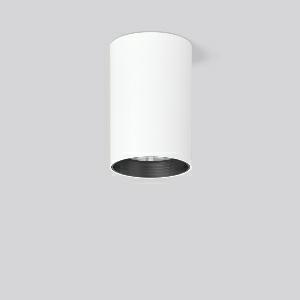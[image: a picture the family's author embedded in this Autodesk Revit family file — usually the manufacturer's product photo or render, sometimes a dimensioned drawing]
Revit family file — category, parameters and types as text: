
# Revit family: heledon_maxi_a_931221_002_3_a406
name_source: partatom
category: Lighting Fixtures
units: mm (PartAtom-declared; Revit-internal decimal feet)

## family parameters
Cut with Voids When Loaded = No
Host = Face
Light Source = No
Part Type = Normal
Room Calculation Point = No
Round Connector Dimension = Use Diameter
Shared = No

## types (1)
- HELEDON maxi A (1 x LED Modul 935, 2800 lm, 3500)
    Apparent Load = 25 VA
    Approval mark = CE
    CIE Flux Codes = 96 100 100 100 100
    Color Rendering = 92
    Color Temperature = 3500
    Default Elevation = 1800 mm
    Description = Series: HELEDON maxi
Cylindrical surface-mounted downlight. Housing: die-cast aluminium, powder-coated. Internal ceiling frame polycarbonate with bayonet mounting. Black plastic ring and recessed LED to prevent glare from the side. Optical assembly with lens made of plastic (polycarbonate) for the best homogeneous light distribution - can be changed without tools. Best colour rendering index Ra>90. Suitable for Ceiling mounting. Easy installation with a separate ceiling frame with bayonet mounting and plug connection. Driver integrated. Connected via plug-in connector. High quality converter without flickering and stroboscopic effect. The following accessories can be mounted without use of tools: interchangeable lenses, decorative glasses, honeycomb louvre, clear and frosted diffusers, white interchangeable plastic ring. 
Colour: traffic white, matt (RAL 9016)
Diameter: 123 mm
Height: 183 mm
Lamp: LED
Socket: without socket
Colour temperature: 3500K
Colour rendering index (CRI): 92
System power: 25 W
Rated luminous flux: 2800 lm
Luminous efficiency: 112 lm/W
Control gear: Regulated power supply
Protection class: I
Type of protection: IP 20
    Height = 183 mm
    Lamp = 1 x LED Modul 935
    Lamp Light Flux = 2800 lm
    Lamp count = 1
    Length = 123 mm
    Lifetime = 50000 h
    Luminous efficacy = 112 lm/W
    Manufacturer = RZB
    ModVariant = No
    Model = 931221.002.3
    Mounting Place = Ceiling
    Mounting Type = Surface mounted
    Number of Poles = 1
    OnlyDefault = Yes
    Power Factor = 1
    Product Name = HELEDON maxi A
    Product group = Surface mounted downlights
    ProductGroupID = 302
    Protection Class = Protection class I
    Protection Degree = IP 20
    RLX_Detail_Level = 1
    RLX_Emergency_Light_Flux = 0 lm
    RLX_Emergency_Type = 0
    RLX_Emergency_Type_DB = No
    RlxData = <blob elided: 98009 chars, md5=9b2dfd3f>
    Socket = socket
    Standby Power = 0 W
    System Light Flux = 2800 lm
    System Power = 25 W
    Type Comments = Product without accessories
    Type Image = 931193.002.jpg
    URL = http://relux.com
    VarID = ---
    Voltage = 230 V
    Voltage Range = 220-240 V
    Weight = 0.00 kg
    Width = 0 mm  [stored 0 ft]

note: [stored X ft] marks values corroborated as IEEE doubles in the binary element streams (Revit-internal decimal feet)

## geometry (parser evidence)
native form markers: Blend x4, Sweep x11
no freeform markers — native parametric forms only
